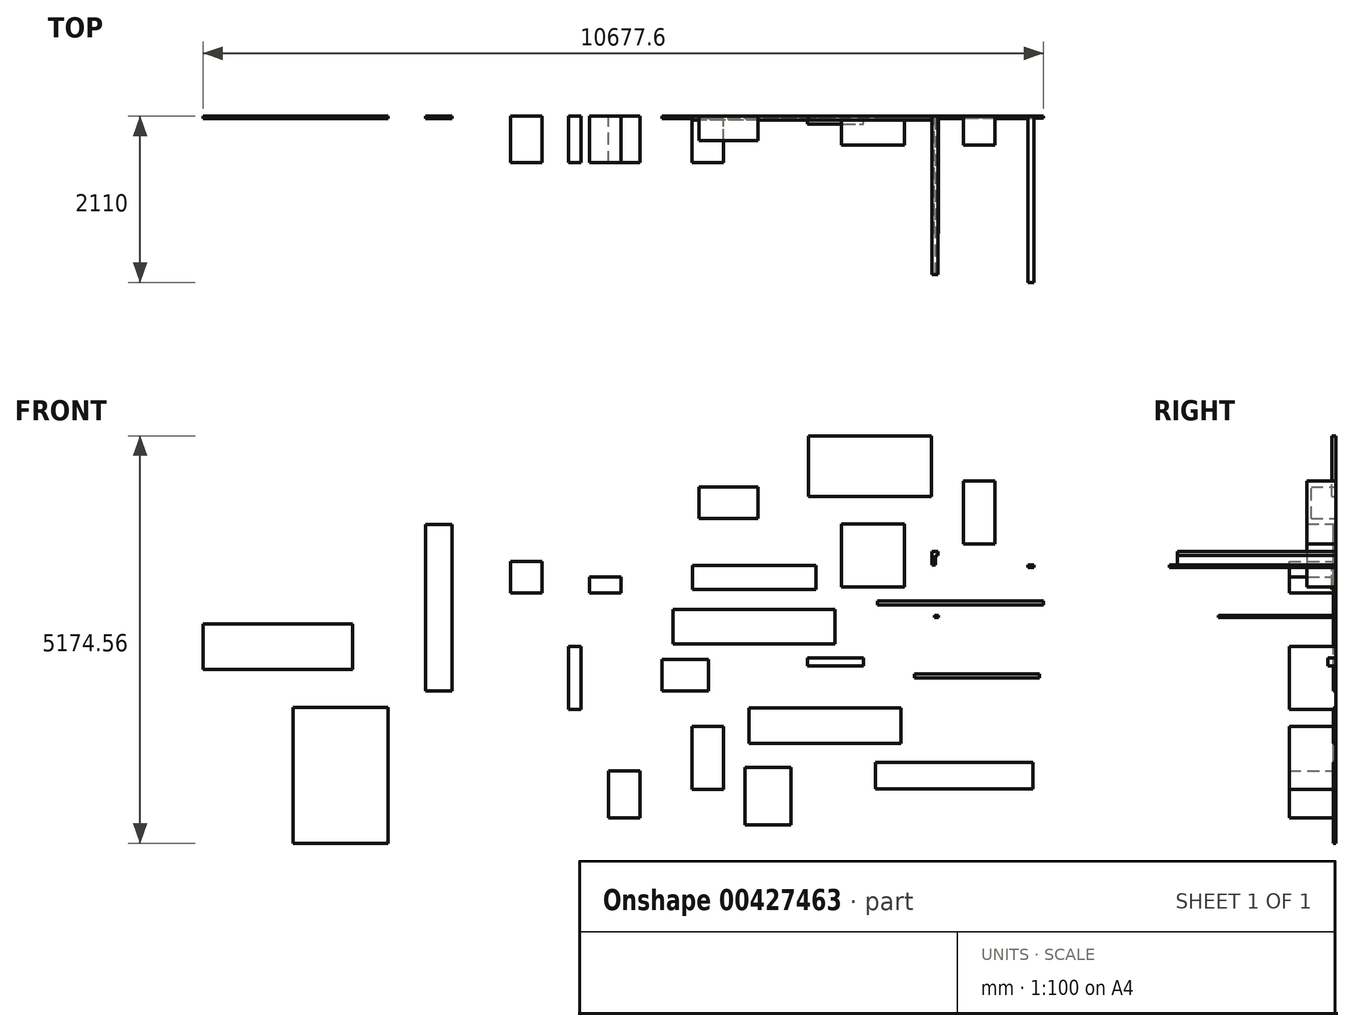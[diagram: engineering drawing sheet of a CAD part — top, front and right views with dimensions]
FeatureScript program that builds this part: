
annotation { "Feature Type Name" : "Feature", "Feature Type Description" : "" }
export const myFeature = defineFeature(function(context is Context, id is Id, definition is map)
    precondition{}
    {
        {
            var Q0;
            Q0=qCreatedBy(makeId("Front.planeOp"),FACE);
            var sketch = newSketch(context, id + "F0", { "sketchPlane" : qUnion([Q0])});
            skLineSegment(sketch, "E0.bottom", {"start": v(-70.34, 315.88) * mm, "end": v(639.66, 315.88) * mm});
            skLineSegment(sketch, "E0.top", {"start": v(-70.34, 415.88) * mm, "end": v(639.66, 415.88) * mm});
            skLineSegment(sketch, "E0.left", {"start": v(-70.34, 315.88) * mm, "end": v(-70.34, 415.88) * mm});
            skLineSegment(sketch, "E0.right", {"start": v(639.66, 315.88) * mm, "end": v(639.66, 415.88) * mm});
            skSolve(sketch);
        }
        {
            var Q0;
            Q0=qSketchRegion(id+"F0",true);
            extrude(context, id + "F1", {"entities" : qUnion([Q0]), "depth" : 100 * mm});
        }
        {
            var Q0;
            Q0=qCreatedBy(makeId("Front.planeOp"),FACE);
            var sketch = newSketch(context, id + "F2", { "sketchPlane" : qUnion([Q0])});
            skLineSegment(sketch, "E1.bottom", {"start": v(2792.12, -1245.36) * mm, "end": v(792.12, -1245.36) * mm});
            skLineSegment(sketch, "E1.top", {"start": v(2792.12, -911.36) * mm, "end": v(792.12, -911.36) * mm});
            skLineSegment(sketch, "E1.left", {"start": v(2792.12, -1245.36) * mm, "end": v(2792.12, -911.36) * mm});
            skLineSegment(sketch, "E1.right", {"start": v(792.12, -1245.36) * mm, "end": v(792.12, -911.36) * mm});
            skPoint(sketch, "E1.middle", {"position": v(1792.12, -1078.36) * mm});
            skSolve(sketch);
        }
        {
            var Q0;
            Q0=qSketchRegion(id+"F2",true);
            extrude(context, id + "F3", {"entities" : qUnion([Q0]), "depth" : 27 * mm});
        }
        {
            var Q0;
            Q0=qCreatedBy(makeId("Front.planeOp"),FACE);
            var sketch = newSketch(context, id + "F4", { "sketchPlane" : qUnion([Q0])});
            skLineSegment(sketch, "E2.bottom", {"start": v(1507.35, 2468.2) * mm, "end": v(-57.65, 2468.2) * mm});
            skLineSegment(sketch, "E2.top", {"start": v(1507.35, 3238.2) * mm, "end": v(-57.65, 3238.2) * mm});
            skLineSegment(sketch, "E2.left", {"start": v(1507.35, 2468.2) * mm, "end": v(1507.35, 3238.2) * mm});
            skLineSegment(sketch, "E2.right", {"start": v(-57.65, 2468.2) * mm, "end": v(-57.65, 3238.2) * mm});
            skPoint(sketch, "E2.middle", {"position": v(724.85, 2853.2) * mm});
            skLineSegment(sketch, "E3.bottom", {"start": v(36.65, 1290.1) * mm, "end": v(-1528.35, 1290.1) * mm});
            skLineSegment(sketch, "E3.top", {"start": v(36.65, 1590.1) * mm, "end": v(-1528.35, 1590.1) * mm});
            skLineSegment(sketch, "E3.left", {"start": v(36.65, 1290.1) * mm, "end": v(36.65, 1590.1) * mm});
            skLineSegment(sketch, "E3.right", {"start": v(-1528.35, 1290.1) * mm, "end": v(-1528.35, 1590.1) * mm});
            skPoint(sketch, "E3.middle", {"position": v(-745.85, 1440.1) * mm});
            skSolve(sketch);
        }
        {
            var Q0;
            Q0=qSketchRegion(id+"F4",true);
            extrude(context, id + "F5", {"entities" : qUnion([Q0]), "depth" : 50 * mm});
        }
        {
            var Q0;
            Q0=qCreatedBy(makeId("Front.planeOp"),FACE);
            var sketch = newSketch(context, id + "F6", { "sketchPlane" : qUnion([Q0])});
            skLineSegment(sketch, "E4", {"start": v(1558.46, 1595.78) * mm, "end": v(1513.46, 1595.78) * mm});
            skLineSegment(sketch, "E5", {"start": v(1513.46, 1595.78) * mm, "end": v(1513.46, 1770.78) * mm});
            skLineSegment(sketch, "E6", {"start": v(1513.46, 1770.78) * mm, "end": v(1588.46, 1770.78) * mm});
            skLineSegment(sketch, "E7", {"start": v(1588.46, 1770.78) * mm, "end": v(1588.46, 1720.78) * mm});
            skLineSegment(sketch, "E8", {"start": v(1588.46, 1720.78) * mm, "end": v(1558.46, 1720.78) * mm});
            skLineSegment(sketch, "E9", {"start": v(1558.46, 1720.78) * mm, "end": v(1558.46, 1595.78) * mm});
            skSolve(sketch);
        }
        {
            var Q0;
            Q0=qSketchRegion(id+"F6",true);
            extrude(context, id + "F7", {"entities" : qUnion([Q0]), "depth" : 2010 * mm});
        }
        {
            var Q0;
            Q0=qCreatedBy(makeId("Front.planeOp"),FACE);
            var sketch = newSketch(context, id + "F8", { "sketchPlane" : qUnion([Q0])});
            skLineSegment(sketch, "E10.bottom", {"start": v(2929.7, 1090.93) * mm, "end": v(819.7, 1090.93) * mm});
            skLineSegment(sketch, "E10.top", {"start": v(2929.7, 1138.93) * mm, "end": v(819.7, 1138.93) * mm});
            skLineSegment(sketch, "E10.left", {"start": v(2929.7, 1090.93) * mm, "end": v(2929.7, 1138.93) * mm});
            skLineSegment(sketch, "E10.right", {"start": v(819.7, 1090.93) * mm, "end": v(819.7, 1138.93) * mm});
            skPoint(sketch, "E10.middle", {"position": v(1874.7, 1114.93) * mm});
            skSolve(sketch);
        }
        {
            var Q0;
            Q0=qSketchRegion(id+"F8",true);
            extrude(context, id + "F9", {"entities" : qUnion([Q0]), "depth" : 24 * mm});
        }
        {
            var Q0;
            Q0=qCreatedBy(makeId("Front.planeOp"),FACE);
            var sketch = newSketch(context, id + "F10", { "sketchPlane" : qUnion([Q0])});
            skLineSegment(sketch, "E11.bottom", {"start": v(2877, 163.53) * mm, "end": v(1288, 163.53) * mm});
            skLineSegment(sketch, "E11.top", {"start": v(2877, 211.53) * mm, "end": v(1288, 211.53) * mm});
            skLineSegment(sketch, "E11.left", {"start": v(2877, 163.53) * mm, "end": v(2877, 211.53) * mm});
            skLineSegment(sketch, "E11.right", {"start": v(1288, 163.53) * mm, "end": v(1288, 211.53) * mm});
            skPoint(sketch, "E11.middle", {"position": v(2082.5, 187.53) * mm});
            skSolve(sketch);
        }
        {
            var Q0;
            Q0=qSketchRegion(id+"F10",true);
            extrude(context, id + "F11", {"entities" : qUnion([Q0]), "depth" : 24 * mm});
        }
        {
            var Q0;
            Q0=qCreatedBy(makeId("Front.planeOp"),FACE);
            var sketch = newSketch(context, id + "F12", { "sketchPlane" : qUnion([Q0])});
            skLineSegment(sketch, "E12.bottom", {"start": v(-5848.88, 271.4) * mm, "end": v(-7747.88, 271.4) * mm});
            skLineSegment(sketch, "E12.top", {"start": v(-5848.88, 851.4) * mm, "end": v(-7747.88, 851.4) * mm});
            skLineSegment(sketch, "E12.left", {"start": v(-5848.88, 271.4) * mm, "end": v(-5848.88, 851.4) * mm});
            skLineSegment(sketch, "E12.right", {"start": v(-7747.88, 271.4) * mm, "end": v(-7747.88, 851.4) * mm});
            skPoint(sketch, "E12.middle", {"position": v(-6798.38, 561.4) * mm});
            skLineSegment(sketch, "E13.bottom", {"start": v(-4585.05, 0) * mm, "end": v(-4919.05, 0) * mm});
            skLineSegment(sketch, "E13.top", {"start": v(-4585.05, 2110) * mm, "end": v(-4919.05, 2110) * mm});
            skLineSegment(sketch, "E13.left", {"start": v(-4585.05, 0) * mm, "end": v(-4585.05, 2110) * mm});
            skLineSegment(sketch, "E13.right", {"start": v(-4919.05, 0) * mm, "end": v(-4919.05, 2110) * mm});
            skPoint(sketch, "E13.middle", {"position": v(-4752.05, 1055) * mm});
            skLineSegment(sketch, "E14.bottom", {"start": v(-5395.23, -1936.35) * mm, "end": v(-6605.51, -1936.35) * mm});
            skLineSegment(sketch, "E14.top", {"start": v(-5395.23, -210.2) * mm, "end": v(-6605.51, -210.2) * mm});
            skLineSegment(sketch, "E14.left", {"start": v(-5395.23, -1936.35) * mm, "end": v(-5395.23, -210.2) * mm});
            skLineSegment(sketch, "E14.right", {"start": v(-6605.51, -1936.35) * mm, "end": v(-6605.51, -210.2) * mm});
            skPoint(sketch, "E14.middle", {"position": v(-6000.37, -1073.28) * mm});
            skSolve(sketch);
        }
        {
            var Q0;
            Q0=qSketchRegion(id+"F12",true);
            extrude(context, id + "F13", {"entities" : qUnion([Q0]), "depth" : 28 * mm});
        }
        {
            var Q0;
            Q0=qCreatedBy(makeId("Front.planeOp"),FACE);
            var sketch = newSketch(context, id + "F14", { "sketchPlane" : qUnion([Q0])});
            skLineSegment(sketch, "E15.bottom", {"start": v(362.1, 2119.75) * mm, "end": v(1162.1, 2119.75) * mm});
            skLineSegment(sketch, "E15.top", {"start": v(362.1, 1319.75) * mm, "end": v(1162.1, 1319.75) * mm});
            skLineSegment(sketch, "E15.left", {"start": v(362.1, 2119.75) * mm, "end": v(362.1, 1319.75) * mm});
            skLineSegment(sketch, "E15.right", {"start": v(1162.1, 2119.75) * mm, "end": v(1162.1, 1319.75) * mm});
            skSolve(sketch);
        }
        {
            var Q0;
            Q0 = qSketchRegion(id + "F14", true);
            extrude(context, id + "F15", {"entities" : qUnion([Q0]), "depth" : 366 * mm});
        }
        {
            var Q0;
            Q0=qCreatedBy(makeId("Front.planeOp"),FACE);
            var sketch = newSketch(context, id + "F16", { "sketchPlane" : qUnion([Q0])});
            skLineSegment(sketch, "E16.bottom", {"start": v(1909.96, 1864.78) * mm, "end": v(2309.96, 1864.78) * mm});
            skLineSegment(sketch, "E16.top", {"start": v(1909.96, 2664.78) * mm, "end": v(2309.96, 2664.78) * mm});
            skLineSegment(sketch, "E16.left", {"start": v(1909.96, 1864.78) * mm, "end": v(1909.96, 2664.78) * mm});
            skLineSegment(sketch, "E16.right", {"start": v(2309.96, 1864.78) * mm, "end": v(2309.96, 2664.78) * mm});
            skSolve(sketch);
        }
        {
            var Q0;
            Q0 = qSketchRegion(id + "F16", true);
            extrude(context, id + "F17", {"entities" : qUnion([Q0]), "depth" : 366 * mm});
        }
        {
            var Q0;
            Q0=qCreatedBy(makeId("Front.planeOp"),FACE);
            var sketch = newSketch(context, id + "F18", { "sketchPlane" : qUnion([Q0])});
            skLineSegment(sketch, "E17.bottom", {"start": v(-1445.88, 2189.41) * mm, "end": v(-695.88, 2189.41) * mm});
            skLineSegment(sketch, "E17.top", {"start": v(-1445.88, 2589.41) * mm, "end": v(-695.88, 2589.41) * mm});
            skLineSegment(sketch, "E17.left", {"start": v(-1445.88, 2189.41) * mm, "end": v(-1445.88, 2589.41) * mm});
            skLineSegment(sketch, "E17.right", {"start": v(-695.88, 2189.41) * mm, "end": v(-695.88, 2589.41) * mm});
            skSolve(sketch);
        }
        {
            var Q0;
            Q0 = qSketchRegion(id + "F18", true);
            extrude(context, id + "F19", {"entities" : qUnion([Q0]), "depth" : 310 * mm});
        }
        {
            var Q0;
            Q0=qCreatedBy(makeId("Front.planeOp"),FACE);
            var sketch = newSketch(context, id + "F20", { "sketchPlane" : qUnion([Q0])});
            skLineSegment(sketch, "E18.bottom", {"start": v(2733.76, 1567.97) * mm, "end": v(2808.76, 1567.97) * mm});
            skLineSegment(sketch, "E18.top", {"start": v(2733.76, 1597.97) * mm, "end": v(2808.76, 1597.97) * mm});
            skLineSegment(sketch, "E18.left", {"start": v(2733.76, 1567.97) * mm, "end": v(2733.76, 1597.97) * mm});
            skLineSegment(sketch, "E18.right", {"start": v(2808.76, 1567.97) * mm, "end": v(2808.76, 1597.97) * mm});
            skSolve(sketch);
        }
        {
            var Q0;
            Q0 = qSketchRegion(id + "F20", true);
            extrude(context, id + "F21", {"entities" : qUnion([Q0]), "depth" : 2110 * mm});
        }
        {
            var Q0;
            Q0=qCreatedBy(makeId("Front.planeOp"),FACE);
            var sketch = newSketch(context, id + "F22", { "sketchPlane" : qUnion([Q0])});
            skLineSegment(sketch, "E19.bottom", {"start": v(-2838.93, 1443.37) * mm, "end": v(-2438.93, 1443.37) * mm});
            skLineSegment(sketch, "E19.top", {"start": v(-2838.93, 1243.37) * mm, "end": v(-2438.93, 1243.37) * mm});
            skLineSegment(sketch, "E19.left", {"start": v(-2838.93, 1443.37) * mm, "end": v(-2838.93, 1243.37) * mm});
            skLineSegment(sketch, "E19.right", {"start": v(-2438.93, 1443.37) * mm, "end": v(-2438.93, 1243.37) * mm});
            skLineSegment(sketch, "E20.bottom", {"start": v(-3438.78, 1242.1) * mm, "end": v(-3838.78, 1242.1) * mm});
            skLineSegment(sketch, "E20.top", {"start": v(-3438.78, 1642.1) * mm, "end": v(-3838.78, 1642.1) * mm});
            skLineSegment(sketch, "E20.left", {"start": v(-3438.78, 1242.1) * mm, "end": v(-3438.78, 1642.1) * mm});
            skLineSegment(sketch, "E20.right", {"start": v(-3838.78, 1242.1) * mm, "end": v(-3838.78, 1642.1) * mm});
            skSolve(sketch);
        }
        {
            var Q0;
            Q0 = qSketchRegion(id + "F22", true);
            extrude(context, id + "F23", {"entities" : qUnion([Q0]), "depth" : 590 * mm});
        }
        {
            var Q0;
            Q0=qCreatedBy(makeId("Front.planeOp"),FACE);
            var sketch = newSketch(context, id + "F24", { "sketchPlane" : qUnion([Q0])});
            skLineSegment(sketch, "E21.bottom", {"start": v(-2596.9, -1617.65) * mm, "end": v(-2196.9, -1617.65) * mm});
            skLineSegment(sketch, "E21.top", {"start": v(-2596.9, -1017.65) * mm, "end": v(-2196.9, -1017.65) * mm});
            skLineSegment(sketch, "E21.left", {"start": v(-2596.9, -1617.65) * mm, "end": v(-2596.9, -1017.65) * mm});
            skLineSegment(sketch, "E21.right", {"start": v(-2196.9, -1617.65) * mm, "end": v(-2196.9, -1017.65) * mm});
            skSolve(sketch);
        }
        {
            var Q0;
            Q0 = qSketchRegion(id + "F24", true);
            extrude(context, id + "F25", {"entities" : qUnion([Q0]), "depth" : 590 * mm});
        }
        {
            var Q0;
            Q0=qCreatedBy(makeId("Front.planeOp"),FACE);
            var sketch = newSketch(context, id + "F26", { "sketchPlane" : qUnion([Q0])});
            skLineSegment(sketch, "E22.bottom", {"start": v(-1324.59, 0) * mm, "end": v(-1914.59, 0) * mm});
            skLineSegment(sketch, "E22.top", {"start": v(-1324.59, 400) * mm, "end": v(-1914.59, 400) * mm});
            skLineSegment(sketch, "E22.left", {"start": v(-1324.59, 0) * mm, "end": v(-1324.59, 400) * mm});
            skLineSegment(sketch, "E22.right", {"start": v(-1914.59, 0) * mm, "end": v(-1914.59, 400) * mm});
            skSolve(sketch);
        }
        {
            var Q0;
            Q0 = qSketchRegion(id + "F26", true);
            extrude(context, id + "F27", {"entities" : qUnion([Q0]), "depth" : 28 * mm});
        }
        {
            var Q0;
            Q0=qCreatedBy(makeId("Front.planeOp"),FACE);
            var sketch = newSketch(context, id + "F28", { "sketchPlane" : qUnion([Q0])});
            skLineSegment(sketch, "E23.bottom", {"start": v(-3107.87, -233.81) * mm, "end": v(-2947.87, -233.81) * mm});
            skLineSegment(sketch, "E23.top", {"start": v(-3107.87, 566.19) * mm, "end": v(-2947.87, 566.19) * mm});
            skLineSegment(sketch, "E23.left", {"start": v(-3107.87, -233.81) * mm, "end": v(-3107.87, 566.19) * mm});
            skLineSegment(sketch, "E23.right", {"start": v(-2947.87, -233.81) * mm, "end": v(-2947.87, 566.19) * mm});
            skSolve(sketch);
        }
        {
            var Q0;
            Q0 = qSketchRegion(id + "F28", true);
            extrude(context, id + "F29", {"entities" : qUnion([Q0]), "depth" : 590 * mm});
        }
        {
            var Q0;
            Q0=qCreatedBy(makeId("Front.planeOp"),FACE);
            var sketch = newSketch(context, id + "F30", { "sketchPlane" : qUnion([Q0])});
            skLineSegment(sketch, "E24.bottom", {"start": v(-1534.1, -1253.8) * mm, "end": v(-1134.1, -1253.8) * mm});
            skLineSegment(sketch, "E24.top", {"start": v(-1534.1, -453.8) * mm, "end": v(-1134.1, -453.8) * mm});
            skLineSegment(sketch, "E24.left", {"start": v(-1534.1, -1253.8) * mm, "end": v(-1534.1, -453.8) * mm});
            skLineSegment(sketch, "E24.right", {"start": v(-1134.1, -1253.8) * mm, "end": v(-1134.1, -453.8) * mm});
            skSolve(sketch);
        }
        {
            var Q0;
            Q0 = qSketchRegion(id + "F30", true);
            extrude(context, id + "F31", {"entities" : qUnion([Q0]), "depth" : 590 * mm});
        }
        {
            var Q0;
            Q0=qCreatedBy(makeId("Front.planeOp"),FACE);
            var sketch = newSketch(context, id + "F32", { "sketchPlane" : qUnion([Q0])});
            skLineSegment(sketch, "E25.bottom", {"start": v(-1778.46, 1035.73) * mm, "end": v(281.54, 1035.73) * mm});
            skLineSegment(sketch, "E25.top", {"start": v(-1778.46, 594.73) * mm, "end": v(281.54, 594.73) * mm});
            skLineSegment(sketch, "E25.left", {"start": v(-1778.46, 1035.73) * mm, "end": v(-1778.46, 594.73) * mm});
            skLineSegment(sketch, "E25.right", {"start": v(281.54, 1035.73) * mm, "end": v(281.54, 594.73) * mm});
            skLineSegment(sketch, "E26.bottom", {"start": v(-815.1, -217.6) * mm, "end": v(1115.9, -217.6) * mm});
            skLineSegment(sketch, "E26.top", {"start": v(-815.1, -667.6) * mm, "end": v(1115.9, -667.6) * mm});
            skLineSegment(sketch, "E26.left", {"start": v(-815.1, -217.6) * mm, "end": v(-815.1, -667.6) * mm});
            skLineSegment(sketch, "E26.right", {"start": v(1115.9, -217.6) * mm, "end": v(1115.9, -667.6) * mm});
            skLineSegment(sketch, "E27.bottom", {"start": v(-866.07, -974.82) * mm, "end": v(-276.07, -974.82) * mm});
            skLineSegment(sketch, "E27.top", {"start": v(-866.07, -1705.82) * mm, "end": v(-276.07, -1705.82) * mm});
            skLineSegment(sketch, "E27.left", {"start": v(-866.07, -974.82) * mm, "end": v(-866.07, -1705.82) * mm});
            skLineSegment(sketch, "E27.right", {"start": v(-276.07, -974.82) * mm, "end": v(-276.07, -1705.82) * mm});
            skSolve(sketch);
        }
        {
            var Q0;
            Q0 = qSketchRegion(id + "F32", true);
            extrude(context, id + "F33", {"entities" : qUnion([Q0]), "depth" : 27 * mm});
        }
        {
            var Q0;
            Q0=qCreatedBy(makeId("Front.planeOp"),FACE);
            var sketch = newSketch(context, id + "F34", { "sketchPlane" : qUnion([Q0])});
            skLineSegment(sketch, "E28.bottom", {"start": v(1541.46, 958.6) * mm, "end": v(1591.46, 958.6) * mm});
            skLineSegment(sketch, "E28.top", {"start": v(1541.46, 928.6) * mm, "end": v(1591.46, 928.6) * mm});
            skLineSegment(sketch, "E28.left", {"start": v(1541.46, 958.6) * mm, "end": v(1541.46, 928.6) * mm});
            skLineSegment(sketch, "E28.right", {"start": v(1591.46, 958.6) * mm, "end": v(1591.46, 928.6) * mm});
            skSolve(sketch);
        }
        {
            var Q0;
            Q0 = qSketchRegion(id + "F34", true);
            extrude(context, id + "F35", {"entities" : qUnion([Q0]), "depth" : 1490 * mm});
        }
    });
